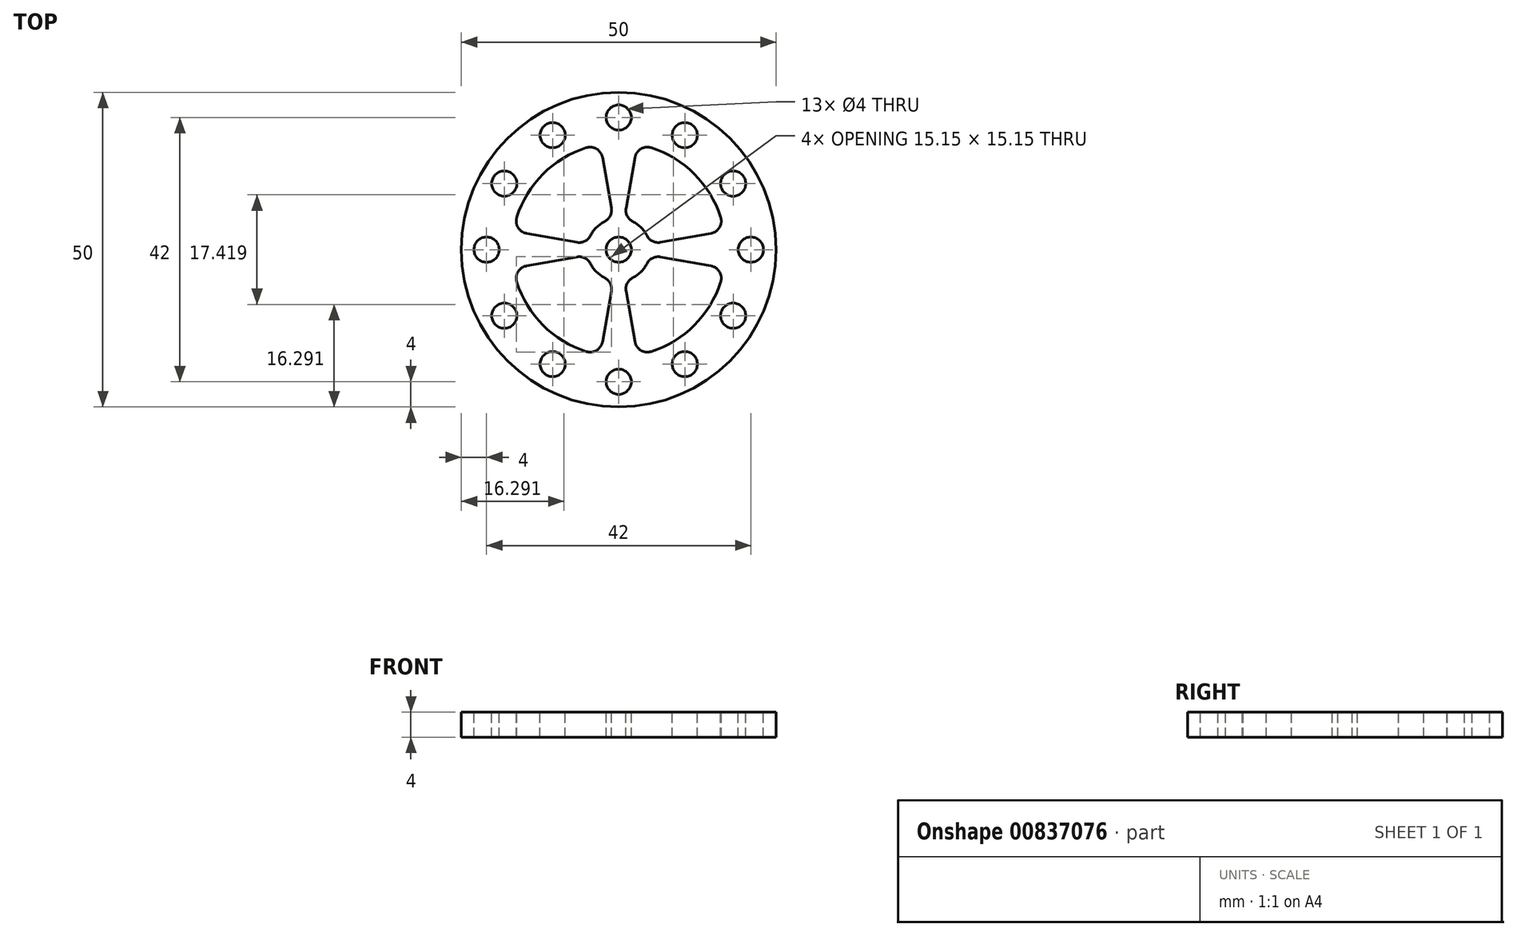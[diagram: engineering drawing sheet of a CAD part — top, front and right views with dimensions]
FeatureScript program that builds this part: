
annotation { "Feature Type Name" : "Feature", "Feature Type Description" : "" }
export const myFeature = defineFeature(function(context is Context, id is Id, definition is map)
    precondition{}
    {
        {
            var Q0;
            Q0=qCreatedBy(makeId("Top.planeOp"),FACE);
            var sketch = newSketch(context, id + "F0", { "sketchPlane" : qUnion([Q0])});
            skCircle(sketch, "E0", {"center": v(0, 0) * mm, "radius": 25 * mm});
            skCircle(sketch, "E1", {"center": v(0, 0) * mm, "radius": 21 * mm, "construction": true});
            skLineSegment(sketch, "E2", {"start": v(0, 0) * mm, "end": v(0, 30.68) * mm, "construction": true});
            skCircle(sketch, "E3", {"center": v(0, 21) * mm, "radius": 2 * mm});
            skCircle(sketch, "E4.1.0", {"center": v(-10.5, 18.19) * mm, "radius": 2 * mm});
            skCircle(sketch, "E4.2.0", {"center": v(-18.19, 10.5) * mm, "radius": 2 * mm});
            skCircle(sketch, "E5.1.3.0", {"center": v(-21, 0) * mm, "radius": 2 * mm});
            skCircle(sketch, "E6.1.4.0", {"center": v(-18.19, -10.5) * mm, "radius": 2 * mm});
            skCircle(sketch, "E6.1.5.0", {"center": v(-10.5, -18.19) * mm, "radius": 2 * mm});
            skCircle(sketch, "E6.1.6.0", {"center": v(0, -21) * mm, "radius": 2 * mm});
            skCircle(sketch, "E6.1.7.0", {"center": v(10.5, -18.19) * mm, "radius": 2 * mm});
            skCircle(sketch, "E7.1.8.0", {"center": v(18.19, -10.5) * mm, "radius": 2 * mm});
            skCircle(sketch, "E7.1.9.0", {"center": v(21, 0) * mm, "radius": 2 * mm});
            skCircle(sketch, "E7.1.10.0", {"center": v(18.19, 10.5) * mm, "radius": 2 * mm});
            skCircle(sketch, "E7.1.11.0", {"center": v(10.5, 18.19) * mm, "radius": 2 * mm});
            skCircle(sketch, "E8", {"center": v(0, 0) * mm, "radius": 2 * mm});
            skSolve(sketch);
        }
        {
            var Q0;
            Q0=makeQuery(id+"F0.imprint","IMPRINT",FACE,{"disambiguationData":[TD([[makeQuery(id+"F0.imprint","IMPRINT",EDGE,{"derivedFrom":sQuery(id+"F0.wireOp",EDGE,"E0")}),1.0]])]});
            extrude(context, id + "F1", {"entities" : qUnion([Q0]), "oppositeDirection" : true, "depth" : 4 * mm, "offsetDistance" : 25 * mm});
        }
        {
            var Q0;
            Q0=makeQuery(id+"F1.opExtrude","CAP_FACE",FACE,{"disambiguationData":[OSD([sQuery(id+"F0.wireOp",EDGE,"E0"),sQuery(id+"F0.wireOp",EDGE,"E3"),sQuery(id+"F0.wireOp",EDGE,"E4.1.0"),sQuery(id+"F0.wireOp",EDGE,"E4.2.0"),sQuery(id+"F0.wireOp",EDGE,"E5.1.3.0"),sQuery(id+"F0.wireOp",EDGE,"E6.1.4.0"),sQuery(id+"F0.wireOp",EDGE,"E6.1.5.0"),sQuery(id+"F0.wireOp",EDGE,"E6.1.6.0"),sQuery(id+"F0.wireOp",EDGE,"E6.1.7.0"),sQuery(id+"F0.wireOp",EDGE,"E7.1.8.0"),sQuery(id+"F0.wireOp",EDGE,"E7.1.9.0"),sQuery(id+"F0.wireOp",EDGE,"E7.1.10.0"),sQuery(id+"F0.wireOp",EDGE,"E7.1.11.0"),sQuery(id+"F0.wireOp",EDGE,"E8")])],"isStart":true});
            var sketch = newSketch(context, id + "F2", { "sketchPlane" : qUnion([Q0])});
            skArc(sketch, "E9", {"start": v(-5.16, 16.2) * mm, "mid": v(-12.02, 12.02) * mm, "end": v(-16.2, 5.16) * mm});
            skLineSegment(sketch, "E10", {"start": v(0, 0) * mm, "end": v(0, 25.99) * mm});
            skLineSegment(sketch, "E11", {"start": v(0, 0) * mm, "end": v(-37.84, 0) * mm});
            skLineSegment(sketch, "E12", {"start": v(-1.16, 6.6) * mm, "end": v(-2.58, 14.64) * mm});
            skLineSegment(sketch, "E13", {"start": v(-6.6, 1.16) * mm, "end": v(-14.64, 2.58) * mm});
            skPoint(sketch, "E14.visualSharp", {"position": v(-16.74, 2.95) * mm});
            skArc(sketch, "E14.filletArc", {"start": v(-16.2, 5.16) * mm, "mid": v(-16, 3.52) * mm, "end": v(-14.64, 2.58) * mm});
            skPoint(sketch, "E15.visualSharp", {"position": v(-2.95, 16.74) * mm});
            skArc(sketch, "E15.filletArc", {"start": v(-2.58, 14.64) * mm, "mid": v(-3.52, 16) * mm, "end": v(-5.16, 16.2) * mm});
            skLineSegment(sketch, "E16.1.0", {"start": v(-6.6, -1.16) * mm, "end": v(-14.64, -2.58) * mm});
            skPoint(sketch, "E16.1.1", {"position": v(-16.74, -2.95) * mm});
            skArc(sketch, "E16.1.2", {"start": v(-16.2, -5.16) * mm, "mid": v(-12.02, -12.02) * mm, "end": v(-5.16, -16.2) * mm});
            skArc(sketch, "E16.1.3", {"start": v(-14.64, -2.58) * mm, "mid": v(-16, -3.52) * mm, "end": v(-16.2, -5.16) * mm});
            skArc(sketch, "E16.1.4", {"start": v(-5.16, -16.2) * mm, "mid": v(-3.52, -16) * mm, "end": v(-2.58, -14.64) * mm});
            skLineSegment(sketch, "E16.1.5", {"start": v(-1.16, -6.6) * mm, "end": v(-2.58, -14.64) * mm});
            skLineSegment(sketch, "E16.2.0", {"start": v(1.16, -6.6) * mm, "end": v(2.58, -14.64) * mm});
            skPoint(sketch, "E16.2.1", {"position": v(2.95, -16.74) * mm});
            skArc(sketch, "E16.2.2", {"start": v(5.16, -16.2) * mm, "mid": v(12.02, -12.02) * mm, "end": v(16.2, -5.16) * mm});
            skArc(sketch, "E16.2.3", {"start": v(2.58, -14.64) * mm, "mid": v(3.52, -16) * mm, "end": v(5.16, -16.2) * mm});
            skArc(sketch, "E16.2.4", {"start": v(16.2, -5.16) * mm, "mid": v(16, -3.52) * mm, "end": v(14.64, -2.58) * mm});
            skLineSegment(sketch, "E16.2.5", {"start": v(6.6, -1.16) * mm, "end": v(14.64, -2.58) * mm});
            skLineSegment(sketch, "E16.3.0", {"start": v(6.6, 1.16) * mm, "end": v(14.64, 2.58) * mm});
            skPoint(sketch, "E16.3.1", {"position": v(16.74, 2.95) * mm});
            skArc(sketch, "E16.3.2", {"start": v(16.2, 5.16) * mm, "mid": v(12.02, 12.02) * mm, "end": v(5.16, 16.2) * mm});
            skArc(sketch, "E16.3.3", {"start": v(14.64, 2.58) * mm, "mid": v(16, 3.52) * mm, "end": v(16.2, 5.16) * mm});
            skArc(sketch, "E16.3.4", {"start": v(5.16, 16.2) * mm, "mid": v(3.52, 16) * mm, "end": v(2.58, 14.64) * mm});
            skLineSegment(sketch, "E16.3.5", {"start": v(1.16, 6.6) * mm, "end": v(2.58, 14.64) * mm});
            skArc(sketch, "E17", {"start": v(-2.24, 4.47) * mm, "mid": v(-3.54, 3.54) * mm, "end": v(-4.47, 2.24) * mm});
            skArc(sketch, "E18.trimOffspring", {"start": v(-4.47, -2.24) * mm, "mid": v(-3.54, -3.54) * mm, "end": v(-2.24, -4.47) * mm});
            skPoint(sketch, "E19.orphan", {"position": v(-0.52, -2.95) * mm});
            skPoint(sketch, "E20.orphan", {"position": v(2.95, -0.52) * mm});
            skPoint(sketch, "E21.orphan", {"position": v(0.52, 2.95) * mm});
            skPoint(sketch, "E22.visualSharp", {"position": v(-0.87, 4.92) * mm});
            skArc(sketch, "E22.filletArc", {"start": v(-2.24, 4.47) * mm, "mid": v(-1.35, 5.36) * mm, "end": v(-1.16, 6.6) * mm});
            skPoint(sketch, "E23.visualSharp", {"position": v(-4.92, 0.87) * mm});
            skArc(sketch, "E23.filletArc", {"start": v(-6.6, 1.16) * mm, "mid": v(-5.36, 1.35) * mm, "end": v(-4.47, 2.24) * mm});
            skPoint(sketch, "E24.visualSharp", {"position": v(-4.92, -0.87) * mm});
            skArc(sketch, "E24.filletArc", {"start": v(-4.47, -2.24) * mm, "mid": v(-5.36, -1.35) * mm, "end": v(-6.6, -1.16) * mm});
            skArc(sketch, "E25.trimOffspring", {"start": v(2.24, -4.47) * mm, "mid": v(3.54, -3.54) * mm, "end": v(4.47, -2.24) * mm});
            skArc(sketch, "E26.trimOffspring", {"start": v(4.47, 2.24) * mm, "mid": v(3.54, 3.54) * mm, "end": v(2.24, 4.47) * mm});
            skPoint(sketch, "E27.visualSharp", {"position": v(-0.87, -4.92) * mm});
            skArc(sketch, "E27.filletArc", {"start": v(-1.16, -6.6) * mm, "mid": v(-1.35, -5.36) * mm, "end": v(-2.24, -4.47) * mm});
            skPoint(sketch, "E28.visualSharp", {"position": v(0.87, -4.92) * mm});
            skArc(sketch, "E28.filletArc", {"start": v(2.24, -4.47) * mm, "mid": v(1.35, -5.36) * mm, "end": v(1.16, -6.6) * mm});
            skPoint(sketch, "E29.visualSharp", {"position": v(4.92, -0.87) * mm});
            skArc(sketch, "E29.filletArc", {"start": v(6.6, -1.16) * mm, "mid": v(5.36, -1.35) * mm, "end": v(4.47, -2.24) * mm});
            skPoint(sketch, "E30.visualSharp", {"position": v(4.92, 0.87) * mm});
            skArc(sketch, "E30.filletArc", {"start": v(4.47, 2.24) * mm, "mid": v(5.36, 1.35) * mm, "end": v(6.6, 1.16) * mm});
            skPoint(sketch, "E31.visualSharp", {"position": v(0.87, 4.92) * mm});
            skArc(sketch, "E31.filletArc", {"start": v(1.16, 6.6) * mm, "mid": v(1.35, 5.36) * mm, "end": v(2.24, 4.47) * mm});
            skSolve(sketch);
        }
        {
            var Q0;
            Q0=makeQuery(id+"F2.imprint","IMPRINT",FACE,{"disambiguationData":[TD([[makeQuery(id+"F2.imprint","IMPRINT",EDGE,{"derivedFrom":sQuery(id+"F2.wireOp",EDGE,"E16.3.0")}),1.0]])]});
            var Q1;
            Q1=makeQuery(id+"F2.imprint","IMPRINT",FACE,{"disambiguationData":[TD([[makeQuery(id+"F2.imprint","IMPRINT",EDGE,{"derivedFrom":sQuery(id+"F2.wireOp",EDGE,"6SLimiCd-Yztc-gV9H-JrcT-Ef1daxfwVjmu")}),-1.0]])]});
            var Q2;
            Q2=makeQuery(id+"F2.imprint","IMPRINT",FACE,{"disambiguationData":[TD([[makeQuery(id+"F2.imprint","IMPRINT",EDGE,{"derivedFrom":sQuery(id+"F2.wireOp",EDGE,"E16.1.0")}),1.0]])]});
            var Q3;
            Q3=makeQuery(id+"F2.imprint","IMPRINT",FACE,{"disambiguationData":[TD([[makeQuery(id+"F2.imprint","IMPRINT",EDGE,{"derivedFrom":sQuery(id+"F2.wireOp",EDGE,"E16.2.0")}),1.0]])]});
            extrude(context, id + "F3", {"entities" : qUnion([Q0, Q1, Q2, Q3]), "operationType" : NewBodyOperationType.REMOVE, "oppositeDirection" : true, "depth" : 25 * mm, "offsetDistance" : 25 * mm});
        }
        {
            var Q0;
            Q0=makeQuery(id+"F2.imprint","IMPRINT",FACE,{"disambiguationData":[TD([[makeQuery(id+"F2.imprint","IMPRINT",EDGE,{"derivedFrom":sQuery(id+"F2.wireOp",EDGE,"E9")}),1.0]])]});
            extrude(context, id + "F4", {"entities" : qUnion([Q0]), "operationType" : NewBodyOperationType.REMOVE, "oppositeDirection" : true, "depth" : 25 * mm, "offsetDistance" : 25 * mm});
        }
    });
